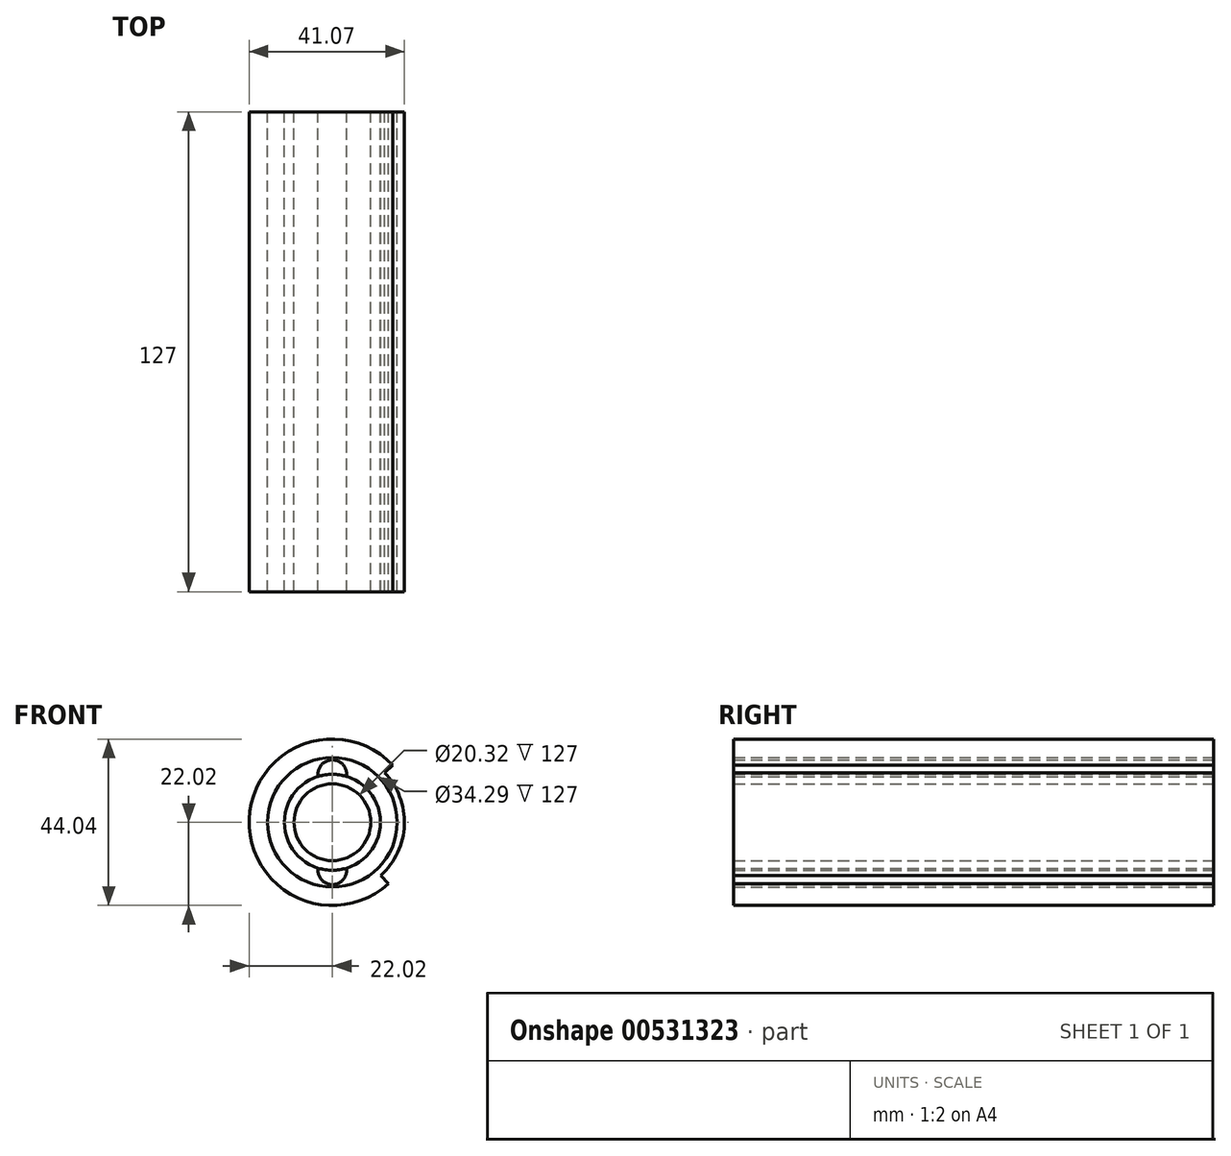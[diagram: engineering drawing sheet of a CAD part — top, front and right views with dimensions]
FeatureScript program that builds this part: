
annotation { "Feature Type Name" : "Feature", "Feature Type Description" : "" }
export const myFeature = defineFeature(function(context is Context, id is Id, definition is map)
    precondition{}
    {
        {
            var Q0;
            Q0=qCreatedBy(makeId("Front.planeOp"),FACE);
            var sketch = newSketch(context, id + "F0", { "sketchPlane" : qUnion([Q0])});
            skCircle(sketch, "E0", {"center": v(0, 0) * mm, "radius": 12.7 * mm});
            skCircle(sketch, "E1", {"center": v(0, 0) * mm, "radius": 19.05 * mm});
            skLineSegment(sketch, "E2", {"start": v(0, 12.7) * mm, "end": v(0, 16.51) * mm});
            skLineSegment(sketch, "E3", {"start": v(0, -12.7) * mm, "end": v(0, -16.51) * mm});
            skArc(sketch, "E4", {"start": v(16, 15.13) * mm, "mid": v(-22, 0.79) * mm, "end": v(14.87, -16.24) * mm});
            skLineSegment(sketch, "E5", {"start": v(14.87, -16.24) * mm, "end": v(12.87, -14.05) * mm});
            skLineSegment(sketch, "E6", {"start": v(16, 15.13) * mm, "end": v(13.84, 13.1) * mm});
            skArc(sketch, "E7", {"start": v(0, 16.51) * mm, "mid": v(-2.89, 15.18) * mm, "end": v(-3.77, 12.13) * mm});
            skArc(sketch, "E8", {"start": v(0, 16.51) * mm, "mid": v(2.89, 15.18) * mm, "end": v(3.77, 12.13) * mm});
            skArc(sketch, "E9", {"start": v(0, -16.51) * mm, "mid": v(2.89, -15.18) * mm, "end": v(3.77, -12.13) * mm});
            skArc(sketch, "E10", {"start": v(0, -16.51) * mm, "mid": v(-2.89, -15.18) * mm, "end": v(-3.77, -12.13) * mm});
            skCircle(sketch, "E11", {"center": v(0, 0) * mm, "radius": 17.15 * mm});
            skCircle(sketch, "E12", {"center": v(0, 0) * mm, "radius": 10.16 * mm});
            skSolve(sketch);
        }
        {
            var Q0;
            Q0=sQuery(id+"F0.wireOp",EDGE,"E0");
            extrude(context, id + "F1", {"bodyType" : ToolBodyType.SURFACE, "surfaceEntities" : qUnion([Q0]), "endBound" : BoundingType.SYMMETRIC, "depth" : 127 * mm, "offsetDistance" : 25.4 * mm});
        }
        {
            var Q0;
            Q0=sQuery(id+"F0.wireOp",EDGE,"E1");
            extrude(context, id + "F2", {"bodyType" : ToolBodyType.SURFACE, "surfaceEntities" : qUnion([Q0]), "endBound" : BoundingType.SYMMETRIC, "depth" : 127 * mm, "offsetDistance" : 25.4 * mm});
        }
        {
            var Q0;
            Q0=sQuery(id+"F0.wireOp",EDGE,"E2");
            extrude(context, id + "F3", {"bodyType" : ToolBodyType.SURFACE, "surfaceEntities" : qUnion([Q0]), "endBound" : BoundingType.SYMMETRIC, "depth" : 127 * mm, "offsetDistance" : 25.4 * mm});
        }
        {
            var Q0;
            Q0=sQuery(id+"F0.wireOp",EDGE,"E3");
            extrude(context, id + "F4", {"bodyType" : ToolBodyType.SURFACE, "surfaceEntities" : qUnion([Q0]), "endBound" : BoundingType.SYMMETRIC, "depth" : 127 * mm, "offsetDistance" : 25.4 * mm});
        }
        {
            var Q0;
            Q0=sQuery(id+"F0.wireOp",EDGE,"E4");
            extrude(context, id + "F5", {"bodyType" : ToolBodyType.SURFACE, "surfaceEntities" : qUnion([Q0]), "endBound" : BoundingType.SYMMETRIC, "depth" : 127 * mm, "offsetDistance" : 25.4 * mm});
        }
        {
            var Q0;
            Q0=sQuery(id+"F0.wireOp",EDGE,"E5");
            extrude(context, id + "F6", {"bodyType" : ToolBodyType.SURFACE, "surfaceEntities" : qUnion([Q0]), "endBound" : BoundingType.SYMMETRIC, "depth" : 127 * mm, "offsetDistance" : 25.4 * mm});
        }
        {
            var Q0;
            Q0=sQuery(id+"F0.wireOp",EDGE,"E6");
            extrude(context, id + "F7", {"bodyType" : ToolBodyType.SURFACE, "surfaceEntities" : qUnion([Q0]), "endBound" : BoundingType.SYMMETRIC, "depth" : 127 * mm, "offsetDistance" : 25.4 * mm});
        }
        {
            var Q0;
            Q0=makeQuery(id+"F0.imprint","IMPRINT",FACE,{"disambiguationData":[TD([[makeQuery(id+"F0.imprint","IMPRINT",EDGE,{"derivedFrom":sQuery(id+"F0.wireOp",EDGE,"E4")}),1.0]])]});
            extrude(context, id + "F8", {"entities" : qUnion([Q0]), "endBound" : BoundingType.SYMMETRIC, "depth" : 127 * mm, "offsetDistance" : 25.4 * mm});
        }
        {
            var Q0;
            {var subQ0=sQuery(id+"F0.wireOp",EDGE,"E2");Q0=makeQuery(id+"F0.imprint","IMPRINT",FACE,{"disambiguationData":[TD([[makeQuery(id+"F0.imprint","IMPRINT",EDGE,{"derivedFrom":subQ0}),1.0]])]});}
            extrude(context, id + "F9", {"entities" : qUnion([Q0]), "endBound" : BoundingType.SYMMETRIC, "depth" : 127 * mm, "offsetDistance" : 25.4 * mm});
        }
        {
            var Q0;
            {var subQ0=sQuery(id+"F0.wireOp",EDGE,"E2");Q0=makeQuery(id+"F0.imprint","IMPRINT",FACE,{"disambiguationData":[TD([[makeQuery(id+"F0.imprint","IMPRINT",EDGE,{"derivedFrom":subQ0}),-1.0]])]});}
            var Q1;
            {var subQ0=sQuery(id+"F0.wireOp",EDGE,"E3");Q1=makeQuery(id+"F0.imprint","IMPRINT",FACE,{"disambiguationData":[TD([[makeQuery(id+"F0.imprint","IMPRINT",EDGE,{"derivedFrom":subQ0}),-1.0]])]});}
            var Q2;
            {var subQ0=sQuery(id+"F0.wireOp",EDGE,"E3");Q2=makeQuery(id+"F0.imprint","IMPRINT",FACE,{"disambiguationData":[TD([[makeQuery(id+"F0.imprint","IMPRINT",EDGE,{"derivedFrom":subQ0}),1.0]])]});}
            extrude(context, id + "F10", {"entities" : qUnion([Q0, Q1, Q2]), "operationType" : NewBodyOperationType.ADD, "endBound" : BoundingType.SYMMETRIC, "depth" : 127 * mm, "offsetDistance" : 25.4 * mm});
        }
        {
            var Q0;
            Q0=makeQuery(id+"F0.imprint","IMPRINT",FACE,{"disambiguationData":[TD([[makeQuery(id+"F0.imprint","IMPRINT",EDGE,{"derivedFrom":sQuery(id+"F0.wireOp",EDGE,"E11")}),-1.0]])]});
            extrude(context, id + "F11", {"entities" : qUnion([Q0]), "operationType" : NewBodyOperationType.ADD, "endBound" : BoundingType.SYMMETRIC, "depth" : 127 * mm, "offsetDistance" : 25.4 * mm});
        }
        {
            var Q0;
            Q0=makeQuery(id+"F0.imprint","IMPRINT",FACE,{"disambiguationData":[TD([[makeQuery(id+"F0.imprint","IMPRINT",EDGE,{"derivedFrom":sQuery(id+"F0.wireOp",EDGE,"E12")}),-1.0]])]});
            extrude(context, id + "F12", {"entities" : qUnion([Q0]), "endBound" : BoundingType.SYMMETRIC, "depth" : 127 * mm, "offsetDistance" : 25.4 * mm});
        }
    });
